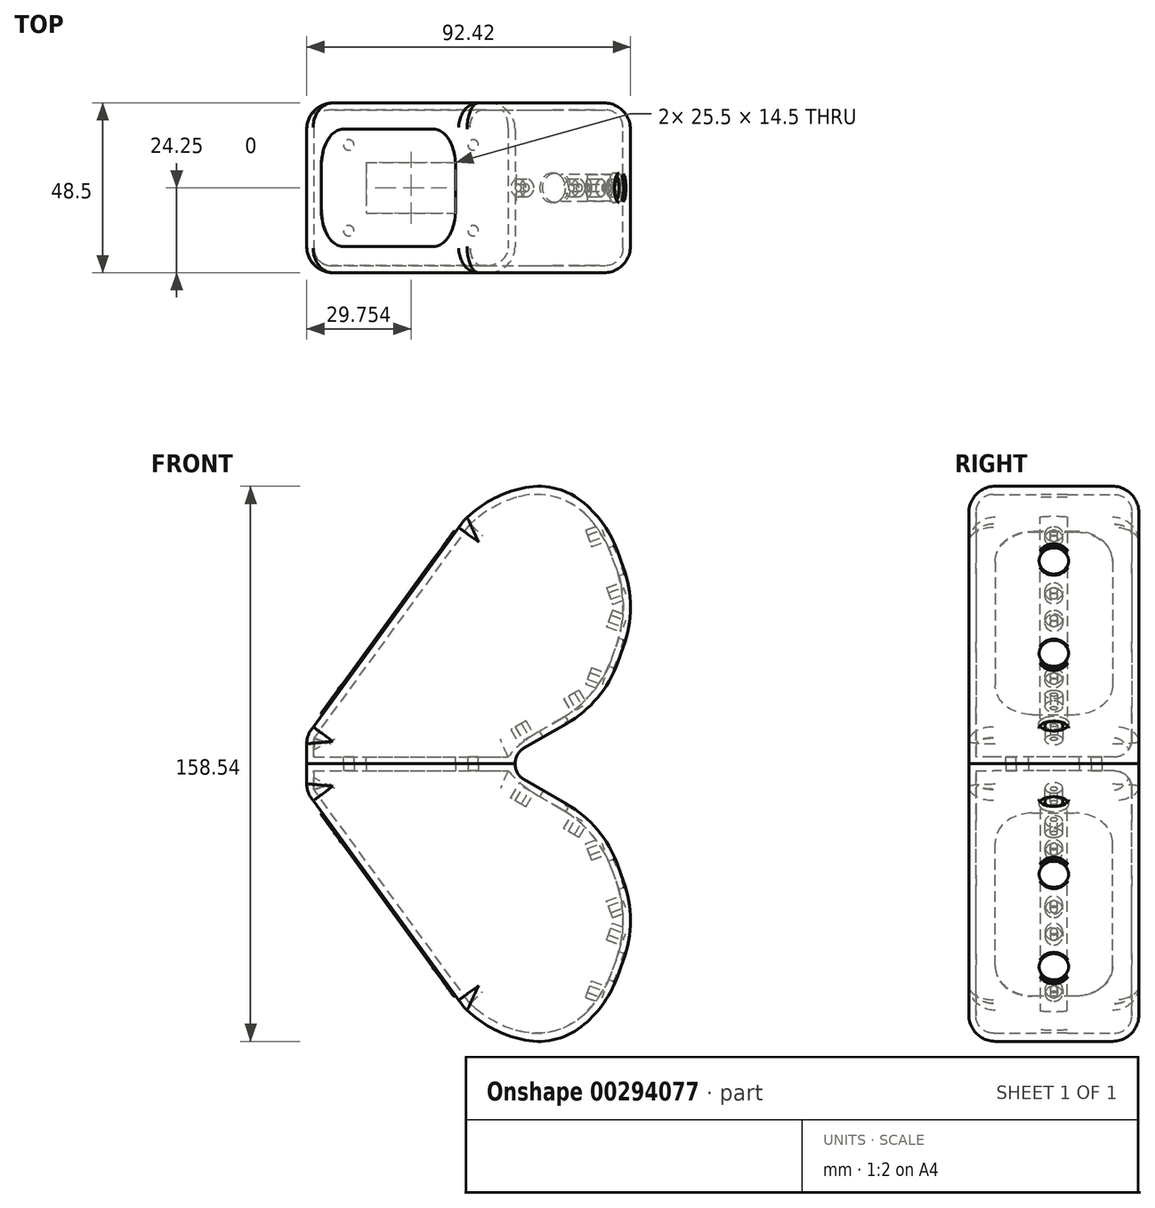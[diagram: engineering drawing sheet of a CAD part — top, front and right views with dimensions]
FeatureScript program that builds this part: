
annotation { "Feature Type Name" : "Feature", "Feature Type Description" : "" }
export const myFeature = defineFeature(function(context is Context, id is Id, definition is map)
    precondition{}
    {
        {
            var Q0;
            Q0=qCreatedBy(makeId("Top.planeOp"),FACE);
            var sketch = newSketch(context, id + "F0", { "sketchPlane" : qUnion([Q0])});
            skLineSegment(sketch, "E0.bottom", {"start": v(-27.46, 14.83) * mm, "end": v(32.04, 14.83) * mm});
            skLineSegment(sketch, "E0.top", {"start": v(-27.46, -33.67) * mm, "end": v(32.04, -33.67) * mm});
            skLineSegment(sketch, "E0.left", {"start": v(-27.46, 14.83) * mm, "end": v(-27.46, -33.67) * mm});
            skLineSegment(sketch, "E0.right", {"start": v(32.04, 14.83) * mm, "end": v(32.04, -33.67) * mm});
            skSolve(sketch);
        }
        {
            var Q0;
            Q0=makeQuery(id+"F0.imprint","IMPRINT",FACE,{"disambiguationData":[TD([[makeQuery(id+"F0.imprint","IMPRINT",EDGE,{"derivedFrom":sQuery(id+"F0.wireOp",EDGE,"E0.bottom")}),-1.0]])]});
            extrude(context, id + "F1", {"entities" : qUnion([Q0]), "depth" : 3 * mm});
        }
        {
            var Q0;
            Q0=makeQuery(id+"F1.opExtrude","SWEPT_FACE",FACE,{"disambiguationData":[OSD([sQuery(id+"F0.wireOp",EDGE,"E0.top")])]});
            var sketch = newSketch(context, id + "F2", { "sketchPlane" : qUnion([Q0])});
            skLineSegment(sketch, "E1", {"start": v(32.04, 3) * mm, "end": v(57.16, 17.5) * mm});
            skLineSegment(sketch, "E2", {"start": v(57.16, 17.5) * mm, "end": v(67.08, 44.75) * mm});
            skLineSegment(sketch, "E3", {"start": v(67.08, 44.75) * mm, "end": v(57.16, 72) * mm});
            skLineSegment(sketch, "E4", {"start": v(44.6, 10.25) * mm, "end": v(61.97, -88.23) * mm, "construction": true});
            skLineSegment(sketch, "E5", {"start": v(44.6, 10.25) * mm, "end": v(121.2, -54.03) * mm, "construction": true});
            skLineSegment(sketch, "E6", {"start": v(62.12, 31.13) * mm, "end": v(138.72, -33.15) * mm, "construction": true});
            skLineSegment(sketch, "E7", {"start": v(62.12, 31.13) * mm, "end": v(162.12, 31.13) * mm, "construction": true});
            skLineSegment(sketch, "E8", {"start": v(62.12, 58.38) * mm, "end": v(162.12, 58.38) * mm, "construction": true});
            skLineSegment(sketch, "E9", {"start": v(62.12, 58.38) * mm, "end": v(138.72, 122.66) * mm, "construction": true});
            skLineSegment(sketch, "E10", {"start": v(32.04, 3) * mm, "end": v(32.04, 5) * mm});
            skLineSegment(sketch, "E11", {"start": v(62.12, 58.38) * mm, "end": v(79.93, 64.86) * mm, "construction": true});
            skLineSegment(sketch, "E12", {"start": v(62.12, 31.13) * mm, "end": v(79.43, 24.82) * mm, "construction": true});
            skLineSegment(sketch, "E13", {"start": v(29.2, 36.93) * mm, "end": v(44.6, 10.25) * mm, "construction": true});
            skLineSegment(sketch, "E14", {"start": v(32.04, 3) * mm, "end": v(32.04, -40.7) * mm, "construction": true});
            skLineSegment(sketch, "E15", {"start": v(32.04, 5) * mm, "end": v(32.04, 48.67) * mm, "construction": true});
            skLineSegment(sketch, "E16", {"start": v(57.16, 72) * mm, "end": v(44.17, 79.5) * mm});
            skLineSegment(sketch, "E17", {"start": v(44.17, 79.5) * mm, "end": v(29.17, 79.5) * mm});
            skLineSegment(sketch, "E18", {"start": v(-27.46, 3) * mm, "end": v(-27.46, 8) * mm});
            skLineSegment(sketch, "E19", {"start": v(29.17, 79.5) * mm, "end": v(17.68, 69.86) * mm});
            skLineSegment(sketch, "E20", {"start": v(17.68, 69.86) * mm, "end": v(-27.46, 8) * mm});
            skSolve(sketch);
        }
        {
            var Q0;
            Q0=makeQuery(id+"F2.imprint","IMPRINT",FACE,{"disambiguationData":[TD([[makeQuery(id+"F2.imprint","IMPRINT",EDGE,{"derivedFrom":sQuery(id+"F2.wireOp",EDGE,"E1")}),1.0]])]});
            var Q1;
            Q1=makeQuery(id+"F1.opExtrude","SWEPT_FACE",FACE,{"disambiguationData":[OSD([sQuery(id+"F0.wireOp",EDGE,"E0.bottom")])]});
            extrude(context, id + "F3", {"entities" : qUnion([Q0]), "operationType" : NewBodyOperationType.ADD, "endBound" : BoundingType.UP_TO_SURFACE, "oppositeDirection" : true, "endBoundEntityFace" : qUnion([Q1]), "depth" : 25 * mm});
        }
        {
            var Q0;
            Q0=makeQuery(id+"F3.opExtrude","SWEPT_FACE",FACE,{"disambiguationData":[OSD([sQuery(id+"F2.wireOp",EDGE,"E20")])]});
            var sketch = newSketch(context, id + "F4", { "sketchPlane" : qUnion([Q0])});
            skLineSegment(sketch, "E21.bottom", {"start": v(25.67, 61.86) * mm, "end": v(-6.83, 61.86) * mm});
            skLineSegment(sketch, "E21.top", {"start": v(25.67, -1.72) * mm, "end": v(-6.83, -1.72) * mm});
            skLineSegment(sketch, "E21.left", {"start": v(25.67, 61.86) * mm, "end": v(25.67, -1.72) * mm});
            skLineSegment(sketch, "E21.right", {"start": v(-6.83, 61.86) * mm, "end": v(-6.83, -1.72) * mm});
            skSolve(sketch);
        }
        {
            var Q0;
            Q0=makeQuery(id+"F4.imprint","IMPRINT",FACE,{"disambiguationData":[TD([[makeQuery(id+"F4.imprint","IMPRINT",EDGE,{"derivedFrom":sQuery(id+"F4.wireOp",EDGE,"E21.bottom")}),1.0]])]});
            extrude(context, id + "F5", {"entities" : qUnion([Q0]), "operationType" : NewBodyOperationType.REMOVE, "oppositeDirection" : true, "depth" : 2 * mm});
        }
        {
            var Q0;
            Q0=makeQuery(id+"F5.boolean.opBoolean","COPY",FACE,{"derivedFrom":makeQuery(id+"F5.opExtrude","CAP_FACE",FACE,{"disambiguationData":[OSD([sQuery(id+"F4.wireOp",EDGE,"E21.bottom"),sQuery(id+"F4.wireOp",EDGE,"E21.top"),sQuery(id+"F4.wireOp",EDGE,"E21.left"),sQuery(id+"F4.wireOp",EDGE,"E21.right")])],"isStart":false})});
            shell(context, id + "F6", {"entities" : qUnion([Q0]), "thickness" : 2 * mm});
        }
        {
            var Q0;
            Q0=makeQuery(id+"F6.opShell","OFFSET_FACE",FACE,{"disambiguationData":[OSD([sQuery(id+"F2.wireOp",EDGE,"E1")])]});
            var sketch = newSketch(context, id + "F7", { "sketchPlane" : qUnion([Q0])});
            skLineSegment(sketch, "E22.0", {"start": v(28.1, 12.83) * mm, "end": v(28.1, -31.67) * mm});
            skLineSegment(sketch, "E23.0", {"start": v(57.52, 12.83) * mm, "end": v(57.52, -31.67) * mm});
            skLineSegment(sketch, "E24", {"start": v(28.1, -9.42) * mm, "end": v(57.52, -9.42) * mm, "construction": true});
            skCircle(sketch, "E25", {"center": v(42.8, -9.42) * mm, "radius": 4.25 * mm});
            skCircle(sketch, "E26", {"center": v(34.06, -9.42) * mm, "radius": 1 * mm});
            skCircle(sketch, "E27", {"center": v(34.06, -9.42) * mm, "radius": 2.5 * mm});
            skCircle(sketch, "E28", {"center": v(51.56, -9.42) * mm, "radius": 1 * mm});
            skCircle(sketch, "E29", {"center": v(51.56, -9.42) * mm, "radius": 2.5 * mm});
            skSolve(sketch);
        }
        {
            var Q0;
            Q0=makeQuery(id+"F6.opShell","OFFSET_FACE",FACE,{"disambiguationData":[OSD([sQuery(id+"F2.wireOp",EDGE,"E2")])]});
            var sketch = newSketch(context, id + "F8", { "sketchPlane" : qUnion([Q0])});
            skLineSegment(sketch, "E30.0", {"start": v(-12.83, 36.72) * mm, "end": v(31.67, 36.72) * mm});
            skLineSegment(sketch, "E31.0", {"start": v(-12.83, 64.27) * mm, "end": v(31.67, 64.27) * mm});
            skLineSegment(sketch, "E32", {"start": v(9.42, 36.72) * mm, "end": v(9.42, 64.27) * mm, "construction": true});
            skCircle(sketch, "E33", {"center": v(9.42, 50.5) * mm, "radius": 4.25 * mm});
            skCircle(sketch, "E34", {"center": v(9.42, 41.74) * mm, "radius": 1 * mm});
            skCircle(sketch, "E35", {"center": v(9.42, 41.74) * mm, "radius": 2.5 * mm});
            skCircle(sketch, "E36", {"center": v(9.42, 59.24) * mm, "radius": 1 * mm});
            skCircle(sketch, "E37", {"center": v(9.42, 59.24) * mm, "radius": 2.5 * mm});
            skSolve(sketch);
        }
        {
            var Q0;
            Q0=makeQuery(id+"F6.opShell","OFFSET_FACE",FACE,{"disambiguationData":[OSD([sQuery(id+"F2.wireOp",EDGE,"E3")])]});
            var sketch = newSketch(context, id + "F9", { "sketchPlane" : qUnion([Q0])});
            skLineSegment(sketch, "E38", {"start": v(9.42, 19.84) * mm, "end": v(9.42, 47.38) * mm, "construction": true});
            skCircle(sketch, "E39", {"center": v(9.42, 33.61) * mm, "radius": 4.25 * mm});
            skCircle(sketch, "E40", {"center": v(9.42, 42.36) * mm, "radius": 1 * mm});
            skCircle(sketch, "E41", {"center": v(9.42, 42.36) * mm, "radius": 2.5 * mm});
            skCircle(sketch, "E42", {"center": v(9.42, 24.86) * mm, "radius": 1 * mm});
            skCircle(sketch, "E43", {"center": v(9.42, 24.86) * mm, "radius": 2.5 * mm});
            skSolve(sketch);
        }
        {
            var Q0;
            Q0=makeQuery(id+"F7.imprint","IMPRINT",FACE,{"disambiguationData":[TD([[makeQuery(id+"F7.imprint","IMPRINT",EDGE,{"derivedFrom":sQuery(id+"F7.wireOp",EDGE,"E25")}),1.0]])]});
            extrude(context, id + "F10", {"entities" : qUnion([Q0]), "operationType" : NewBodyOperationType.REMOVE, "oppositeDirection" : true, "depth" : 25 * mm});
        }
        {
            var Q0;
            Q0=makeQuery(id+"F8.imprint","IMPRINT",FACE,{"disambiguationData":[TD([[makeQuery(id+"F8.imprint","IMPRINT",EDGE,{"derivedFrom":sQuery(id+"F8.wireOp",EDGE,"E33")}),1.0]])]});
            extrude(context, id + "F11", {"entities" : qUnion([Q0]), "operationType" : NewBodyOperationType.REMOVE, "oppositeDirection" : true, "depth" : 25 * mm});
        }
        {
            var Q0;
            Q0=makeQuery(id+"F9.imprint","IMPRINT",FACE,{"disambiguationData":[TD([[makeQuery(id+"F9.imprint","IMPRINT",EDGE,{"derivedFrom":sQuery(id+"F9.wireOp",EDGE,"E39")}),1.0]])]});
            extrude(context, id + "F12", {"entities" : qUnion([Q0]), "operationType" : NewBodyOperationType.REMOVE, "oppositeDirection" : true, "depth" : 25 * mm});
        }
        {
            var Q0;
            Q0=makeQuery(id+"F7.imprint","IMPRINT",FACE,{"disambiguationData":[TD([[makeQuery(id+"F7.imprint","IMPRINT",EDGE,{"derivedFrom":sQuery(id+"F7.wireOp",EDGE,"E26")}),-1.0]])]});
            var Q1;
            Q1=makeQuery(id+"F7.imprint","IMPRINT",FACE,{"disambiguationData":[TD([[makeQuery(id+"F7.imprint","IMPRINT",EDGE,{"derivedFrom":sQuery(id+"F7.wireOp",EDGE,"E28")}),-1.0]])]});
            extrude(context, id + "F13", {"entities" : qUnion([Q0, Q1]), "operationType" : NewBodyOperationType.ADD, "depth" : 4.5 * mm});
        }
        {
            var Q0;
            Q0=makeQuery(id+"F8.imprint","IMPRINT",FACE,{"disambiguationData":[TD([[makeQuery(id+"F8.imprint","IMPRINT",EDGE,{"derivedFrom":sQuery(id+"F8.wireOp",EDGE,"E34")}),-1.0]])]});
            var Q1;
            Q1=makeQuery(id+"F8.imprint","IMPRINT",FACE,{"disambiguationData":[TD([[makeQuery(id+"F8.imprint","IMPRINT",EDGE,{"derivedFrom":sQuery(id+"F8.wireOp",EDGE,"E36")}),-1.0]])]});
            extrude(context, id + "F14", {"entities" : qUnion([Q0, Q1]), "operationType" : NewBodyOperationType.ADD, "depth" : 4.5 * mm});
        }
        {
            var Q0;
            Q0=makeQuery(id+"F9.imprint","IMPRINT",FACE,{"disambiguationData":[TD([[makeQuery(id+"F9.imprint","IMPRINT",EDGE,{"derivedFrom":sQuery(id+"F9.wireOp",EDGE,"E42")}),-1.0]])]});
            var Q1;
            Q1=makeQuery(id+"F9.imprint","IMPRINT",FACE,{"disambiguationData":[TD([[makeQuery(id+"F9.imprint","IMPRINT",EDGE,{"derivedFrom":sQuery(id+"F9.wireOp",EDGE,"E40")}),-1.0]])]});
            extrude(context, id + "F15", {"entities" : qUnion([Q0, Q1]), "operationType" : NewBodyOperationType.ADD, "depth" : 4.5 * mm});
        }
        {
            var Q0;
            Q0=makeQuery(id+"F6.opShell","OFFSET_FACE",FACE,{"disambiguationData":[OSD([sQuery(id+"F0.wireOp",EDGE,"E0.bottom"),sQuery(id+"F0.wireOp",EDGE,"E0.top"),sQuery(id+"F0.wireOp",EDGE,"E0.left"),sQuery(id+"F0.wireOp",EDGE,"E0.right")])]});
            var sketch = newSketch(context, id + "F16", { "sketchPlane" : qUnion([Q0])});
            skLineSegment(sketch, "E44.bottom", {"start": v(-10.46, -2.17) * mm, "end": v(15.04, -2.17) * mm});
            skLineSegment(sketch, "E44.top", {"start": v(-10.46, -16.67) * mm, "end": v(15.04, -16.67) * mm});
            skLineSegment(sketch, "E44.left", {"start": v(-10.46, -2.17) * mm, "end": v(-10.46, -16.67) * mm});
            skLineSegment(sketch, "E44.right", {"start": v(15.04, -2.17) * mm, "end": v(15.04, -16.67) * mm});
            skSolve(sketch);
        }
        {
            var Q0;
            Q0=makeQuery(id+"F16.imprint","IMPRINT",FACE,{"disambiguationData":[TD([[makeQuery(id+"F16.imprint","IMPRINT",EDGE,{"derivedFrom":sQuery(id+"F16.wireOp",EDGE,"E44.bottom")}),-1.0]])]});
            extrude(context, id + "F17", {"entities" : qUnion([Q0]), "operationType" : NewBodyOperationType.REMOVE, "oppositeDirection" : true, "depth" : 25 * mm});
        }
        {
            var Q0;
            Q0=makeQuery(id+"F6.opShell","OFFSET_EDGE",EDGE,{"disambiguationData":[OSD([sQuery(id+"F2.wireOp",EDGE,"E1"),sQuery(id+"F2.wireOp",EDGE,"E2")])]});
            var Q1;
            Q1=makeQuery(id+"F6.opShell","OFFSET_EDGE",EDGE,{"disambiguationData":[OSD([sQuery(id+"F2.wireOp",EDGE,"E2"),sQuery(id+"F2.wireOp",EDGE,"E3")])]});
            var Q2;
            Q2=makeQuery(id+"F6.opShell","OFFSET_EDGE",EDGE,{"disambiguationData":[OSD([sQuery(id+"F2.wireOp",EDGE,"E3"),sQuery(id+"F2.wireOp",EDGE,"E16")])]});
            var Q3;
            Q3=makeQuery(id+"F3.opExtrude","SWEPT_EDGE",EDGE,{"disambiguationData":[OSD([sQuery(id+"F2.wireOp",EDGE,"E1"),sQuery(id+"F2.wireOp",EDGE,"E2")])]});
            var Q4;
            Q4=makeQuery(id+"F3.opExtrude","SWEPT_EDGE",EDGE,{"disambiguationData":[OSD([sQuery(id+"F2.wireOp",EDGE,"E2"),sQuery(id+"F2.wireOp",EDGE,"E3")])]});
            var Q5;
            Q5=makeQuery(id+"F3.opExtrude","SWEPT_EDGE",EDGE,{"disambiguationData":[OSD([sQuery(id+"F2.wireOp",EDGE,"E3"),sQuery(id+"F2.wireOp",EDGE,"E16")])]});
            var Q6;
            Q6=makeQuery(id+"F6.opShell","OFFSET_EDGE",EDGE,{"disambiguationData":[OSD([sQuery(id+"F0.wireOp",EDGE,"E0.top"),sQuery(id+"F0.wireOp",EDGE,"E0.right"),sQuery(id+"F2.wireOp",EDGE,"E1")])]});
            var Q7;
            {var subQ0=sQuery(id+"F2.wireOp",EDGE,"E1");var subQ1=sQuery(id+"F0.wireOp",EDGE,"E0.right");Q7=makeQuery(id+"F20.opFillet","BLEND_EDGE",EDGE,{"blendedFrom":[makeQuery(id+"F3.boolean.opBoolean","MERGE",EDGE,{"derivedFrom":[makeQuery(id+"F1.opExtrude","CAP_EDGE",EDGE,{"disambiguationData":[OSD([subQ1])],"isStart":false}),makeQuery(id+"F3.opExtrude","SWEPT_EDGE",EDGE,{"disambiguationData":[OSD([sQuery(id+"F0.wireOp",EDGE,"E0.top"),subQ1,subQ0])]})]}),makeQuery(id+"F3.opExtrude","SWEPT_FACE",FACE,{"disambiguationData":[OSD([subQ0])]})],"blendedInto":[makeQuery(id+"F3.opExtrude","SWEPT_FACE",FACE,{"disambiguationData":[OSD([subQ0])]})]});}
            var Q8;
            Q8=makeQuery(id+"F3.opExtrude","SWEPT_EDGE",EDGE,{"disambiguationData":[OSD([sQuery(id+"F2.wireOp",EDGE,"E17"),sQuery(id+"F2.wireOp",EDGE,"E19")])]});
            var Q9;
            Q9=makeQuery(id+"F6.opShell","OFFSET_EDGE",EDGE,{"disambiguationData":[OSD([sQuery(id+"F2.wireOp",EDGE,"E17"),sQuery(id+"F2.wireOp",EDGE,"E19")])]});
            fillet(context, id + "F18", {"entities" : qUnion([Q0, Q1, Q2, Q3, Q4, Q5, Q6, Q7, Q8, Q9]), "radius" : 33 * mm, "tangentPropagation" : true, "allowEdgeOverflow" : false});
        }
        {
            var Q0;
            Q0=makeQuery(id+"F6.opShell","OFFSET_EDGE",EDGE,{"disambiguationData":[OSD([sQuery(id+"F2.wireOp",EDGE,"E16"),sQuery(id+"F2.wireOp",EDGE,"E17")])]});
            var Q1;
            Q1=makeQuery(id+"F3.opExtrude","SWEPT_EDGE",EDGE,{"disambiguationData":[OSD([sQuery(id+"F2.wireOp",EDGE,"E16"),sQuery(id+"F2.wireOp",EDGE,"E17")])]});
            fillet(context, id + "F19", {"entities" : qUnion([Q0, Q1]), "radius" : 20 * mm, "tangentPropagation" : true, "allowEdgeOverflow" : false});
        }
        {
            var Q0;
            {var subQ0=sQuery(id+"F0.wireOp",EDGE,"E0.right");Q0=makeQuery(id+"F3.boolean.opBoolean","MERGE",EDGE,{"derivedFrom":[makeQuery(id+"F1.opExtrude","CAP_EDGE",EDGE,{"disambiguationData":[OSD([subQ0])],"isStart":false}),makeQuery(id+"F3.opExtrude","SWEPT_EDGE",EDGE,{"disambiguationData":[OSD([sQuery(id+"F0.wireOp",EDGE,"E0.top"),subQ0,sQuery(id+"F2.wireOp",EDGE,"E1")])]})]});}
            var Q1;
            Q1=makeQuery(id+"F6.opShell","OFFSET_EDGE",EDGE,{"disambiguationData":[OSD([sQuery(id+"F2.wireOp",EDGE,"E1")])]});
            var Q2;
            Q2=makeQuery(id+"F6.opShell","OFFSET_EDGE",EDGE,{"disambiguationData":[OSD([sQuery(id+"F0.wireOp",EDGE,"E0.bottom"),sQuery(id+"F2.wireOp",EDGE,"E1")])]});
            var Q3;
            Q3=makeQuery(id+"F6.opShell","OFFSET_EDGE",EDGE,{"disambiguationData":[OSD([sQuery(id+"F0.wireOp",EDGE,"E0.bottom"),sQuery(id+"F0.wireOp",EDGE,"E0.right")])]});
            var Q4;
            Q4=makeQuery(id+"F6.opShell","OFFSET_EDGE",EDGE,{"disambiguationData":[OSD([sQuery(id+"F0.wireOp",EDGE,"E0.top"),sQuery(id+"F0.wireOp",EDGE,"E0.right")])]});
            var Q5;
            Q5=makeQuery(id+"F6.opShell","OFFSET_EDGE",EDGE,{"disambiguationData":[OSD([sQuery(id+"F0.wireOp",EDGE,"E0.bottom"),sQuery(id+"F2.wireOp",EDGE,"E2")])]});
            var Q6;
            Q6=makeQuery(id+"F6.opShell","OFFSET_EDGE",EDGE,{"disambiguationData":[OSD([sQuery(id+"F0.wireOp",EDGE,"E0.bottom"),sQuery(id+"F2.wireOp",EDGE,"E3")])]});
            var Q7;
            Q7=makeQuery(id+"F6.opShell","OFFSET_EDGE",EDGE,{"disambiguationData":[OSD([sQuery(id+"F0.wireOp",EDGE,"E0.bottom"),sQuery(id+"F2.wireOp",EDGE,"E16")])]});
            var Q8;
            Q8=makeQuery(id+"F6.opShell","OFFSET_EDGE",EDGE,{"disambiguationData":[OSD([sQuery(id+"F0.wireOp",EDGE,"E0.bottom"),sQuery(id+"F2.wireOp",EDGE,"E17")])]});
            var Q9;
            Q9=makeQuery(id+"F6.opShell","OFFSET_EDGE",EDGE,{"disambiguationData":[OSD([sQuery(id+"F0.wireOp",EDGE,"E0.bottom"),sQuery(id+"F0.wireOp",EDGE,"E0.left"),sQuery(id+"F2.wireOp",EDGE,"E18")])]});
            var Q10;
            Q10=makeQuery(id+"F6.opShell","OFFSET_EDGE",EDGE,{"disambiguationData":[OSD([sQuery(id+"F0.wireOp",EDGE,"E0.top"),sQuery(id+"F0.wireOp",EDGE,"E0.left"),sQuery(id+"F2.wireOp",EDGE,"E18")])]});
            var Q11;
            Q11=makeQuery(id+"F6.opShell","OFFSET_EDGE",EDGE,{"disambiguationData":[OSD([sQuery(id+"F2.wireOp",EDGE,"E2")])]});
            var Q12;
            Q12=makeQuery(id+"F6.opShell","OFFSET_EDGE",EDGE,{"disambiguationData":[OSD([sQuery(id+"F2.wireOp",EDGE,"E3")])]});
            var Q13;
            Q13=makeQuery(id+"F6.opShell","OFFSET_EDGE",EDGE,{"disambiguationData":[OSD([sQuery(id+"F2.wireOp",EDGE,"E16")])]});
            var Q14;
            Q14=makeQuery(id+"F6.opShell","OFFSET_EDGE",EDGE,{"disambiguationData":[OSD([sQuery(id+"F2.wireOp",EDGE,"E17")])]});
            var Q15;
            {var subQ0=sQuery(id+"F2.wireOp",EDGE,"E16");Q15=makeQuery(id+"F18.opFillet","BLEND_EDGE",EDGE,{"disambiguationData":[OD(0.0)],"blendedFrom":[makeQuery(id+"F6.opShell","OFFSET_EDGE",EDGE,{"disambiguationData":[OSD([sQuery(id+"F2.wireOp",EDGE,"E3"),subQ0])]}),makeQuery(id+"F6.opShell","OFFSET_EDGE",EDGE,{"disambiguationData":[OSD([subQ0,sQuery(id+"F2.wireOp",EDGE,"E17")])]})],"blendedInto":[]});}
            var Q16;
            Q16=makeQuery(id+"F6.opShell","OFFSET_EDGE",EDGE,{"disambiguationData":[OSD([sQuery(id+"F2.wireOp",EDGE,"E20")])]});
            var Q17;
            {var subQ0=sQuery(id+"F2.wireOp",EDGE,"E19");var subQ1=sQuery(id+"F2.wireOp",EDGE,"E17");Q17=makeQuery(id+"F18.opFillet","BLEND_EDGE",EDGE,{"blendedFrom":[makeQuery(id+"F6.opShell","OFFSET_EDGE",EDGE,{"disambiguationData":[OSD([subQ1,subQ0])]}),makeQuery(id+"F6.opShell","OFFSET_FACE",FACE,{"disambiguationData":[OSD([sQuery(id+"F0.wireOp",EDGE,"E0.top"),sQuery(id+"F2.wireOp",EDGE,"E1"),sQuery(id+"F2.wireOp",EDGE,"E2"),sQuery(id+"F2.wireOp",EDGE,"E3"),sQuery(id+"F2.wireOp",EDGE,"E16"),subQ1,sQuery(id+"F2.wireOp",EDGE,"E18"),subQ0,sQuery(id+"F2.wireOp",EDGE,"E20")])]})],"blendedInto":[makeQuery(id+"F6.opShell","OFFSET_FACE",FACE,{"disambiguationData":[OSD([sQuery(id+"F0.wireOp",EDGE,"E0.top"),sQuery(id+"F2.wireOp",EDGE,"E1"),sQuery(id+"F2.wireOp",EDGE,"E2"),sQuery(id+"F2.wireOp",EDGE,"E3"),sQuery(id+"F2.wireOp",EDGE,"E16"),subQ1,sQuery(id+"F2.wireOp",EDGE,"E18"),subQ0,sQuery(id+"F2.wireOp",EDGE,"E20")])]})]});}
            var Q18;
            Q18=makeQuery(id+"F6.opShell","OFFSET_EDGE",EDGE,{"disambiguationData":[OSD([sQuery(id+"F0.wireOp",EDGE,"E0.bottom"),sQuery(id+"F2.wireOp",EDGE,"E20")])]});
            var Q19;
            Q19=makeQuery(id+"F18.opFillet","BLEND_EDGE",EDGE,{"blendedFrom":[makeQuery(id+"F6.opShell","OFFSET_EDGE",EDGE,{"disambiguationData":[OSD([sQuery(id+"F2.wireOp",EDGE,"E17"),sQuery(id+"F2.wireOp",EDGE,"E19")])]}),makeQuery(id+"F6.opShell","OFFSET_FACE",FACE,{"disambiguationData":[OSD([sQuery(id+"F0.wireOp",EDGE,"E0.bottom")])]})],"blendedInto":[makeQuery(id+"F6.opShell","OFFSET_FACE",FACE,{"disambiguationData":[OSD([sQuery(id+"F0.wireOp",EDGE,"E0.bottom")])]})]});
            var Q20;
            Q20=makeQuery(id+"F18.opFillet","BLEND_EDGE",EDGE,{"blendedFrom":[makeQuery(id+"F6.opShell","OFFSET_EDGE",EDGE,{"disambiguationData":[OSD([sQuery(id+"F2.wireOp",EDGE,"E16"),sQuery(id+"F2.wireOp",EDGE,"E17")])]}),makeQuery(id+"F6.opShell","OFFSET_FACE",FACE,{"disambiguationData":[OSD([sQuery(id+"F0.wireOp",EDGE,"E0.bottom")])]})],"blendedInto":[makeQuery(id+"F6.opShell","OFFSET_FACE",FACE,{"disambiguationData":[OSD([sQuery(id+"F0.wireOp",EDGE,"E0.bottom")])]})]});
            var Q21;
            {var subQ0=sQuery(id+"F2.wireOp",EDGE,"E17");var subQ1=sQuery(id+"F2.wireOp",EDGE,"E16");Q21=makeQuery(id+"F18.opFillet","BLEND_EDGE",EDGE,{"blendedFrom":[makeQuery(id+"F6.opShell","OFFSET_EDGE",EDGE,{"disambiguationData":[OSD([subQ1,subQ0])]}),makeQuery(id+"F6.opShell","OFFSET_FACE",FACE,{"disambiguationData":[OSD([sQuery(id+"F0.wireOp",EDGE,"E0.top"),sQuery(id+"F2.wireOp",EDGE,"E1"),sQuery(id+"F2.wireOp",EDGE,"E2"),sQuery(id+"F2.wireOp",EDGE,"E3"),subQ1,subQ0,sQuery(id+"F2.wireOp",EDGE,"E18"),sQuery(id+"F2.wireOp",EDGE,"E19"),sQuery(id+"F2.wireOp",EDGE,"E20")])]})],"blendedInto":[makeQuery(id+"F6.opShell","OFFSET_FACE",FACE,{"disambiguationData":[OSD([sQuery(id+"F0.wireOp",EDGE,"E0.top"),sQuery(id+"F2.wireOp",EDGE,"E1"),sQuery(id+"F2.wireOp",EDGE,"E2"),sQuery(id+"F2.wireOp",EDGE,"E3"),subQ1,subQ0,sQuery(id+"F2.wireOp",EDGE,"E18"),sQuery(id+"F2.wireOp",EDGE,"E19"),sQuery(id+"F2.wireOp",EDGE,"E20")])]})]});}
            fillet(context, id + "F20", {"entities" : qUnion([Q0, Q1, Q2, Q3, Q4, Q5, Q6, Q7, Q8, Q9, Q10, Q11, Q12, Q13, Q14, Q15, Q16, Q17, Q18, Q19, Q20, Q21]), "radius" : 5 * mm, "tangentPropagation" : true, "allowEdgeOverflow" : false});
        }
        {
            var Q0;
            {var subQ0=sQuery(id+"F0.wireOp",EDGE,"E0.bottom");var subQ1=sQuery(id+"F0.wireOp",EDGE,"E0.right");Q0=makeQuery(id+"F20.opFillet","BLEND_EDGE",EDGE,{"blendedFrom":[makeQuery(id+"F3.boolean.opBoolean","MERGE",EDGE,{"derivedFrom":[makeQuery(id+"F1.opExtrude","CAP_EDGE",EDGE,{"disambiguationData":[OSD([subQ1])],"isStart":false}),makeQuery(id+"F3.opExtrude","SWEPT_EDGE",EDGE,{"disambiguationData":[OSD([sQuery(id+"F0.wireOp",EDGE,"E0.top"),subQ1,sQuery(id+"F2.wireOp",EDGE,"E1")])]})]}),makeQuery(id+"F3.boolean.opBoolean","MERGE",FACE,{"derivedFrom":[makeQuery(id+"F1.opExtrude","SWEPT_FACE",FACE,{"disambiguationData":[OSD([subQ0])]}),makeQuery(id+"F3.opExtrude","CAP_FACE",FACE,{"disambiguationData":[OSD([subQ0])],"isStart":false})]})],"blendedInto":[makeQuery(id+"F3.boolean.opBoolean","MERGE",FACE,{"derivedFrom":[makeQuery(id+"F1.opExtrude","SWEPT_FACE",FACE,{"disambiguationData":[OSD([subQ0])]}),makeQuery(id+"F3.opExtrude","CAP_FACE",FACE,{"disambiguationData":[OSD([subQ0])],"isStart":false})]})]});}
            var Q1;
            {var subQ0=sQuery(id+"F2.wireOp",EDGE,"E1");var subQ1=sQuery(id+"F0.wireOp",EDGE,"E0.top");var subQ2=sQuery(id+"F0.wireOp",EDGE,"E0.right");Q1=makeQuery(id+"F20.opFillet","BLEND_EDGE",EDGE,{"blendedFrom":[makeQuery(id+"F3.boolean.opBoolean","MERGE",EDGE,{"derivedFrom":[makeQuery(id+"F1.opExtrude","CAP_EDGE",EDGE,{"disambiguationData":[OSD([subQ2])],"isStart":false}),makeQuery(id+"F3.opExtrude","SWEPT_EDGE",EDGE,{"disambiguationData":[OSD([subQ1,subQ2,subQ0])]})]}),makeQuery(id+"F3.boolean.opBoolean","MERGE",FACE,{"derivedFrom":[makeQuery(id+"F1.opExtrude","SWEPT_FACE",FACE,{"disambiguationData":[OSD([subQ1])]}),makeQuery(id+"F3.opExtrude","CAP_FACE",FACE,{"disambiguationData":[OSD([subQ1,subQ0,sQuery(id+"F2.wireOp",EDGE,"E2"),sQuery(id+"F2.wireOp",EDGE,"E3"),sQuery(id+"F2.wireOp",EDGE,"E16"),sQuery(id+"F2.wireOp",EDGE,"E17"),sQuery(id+"F2.wireOp",EDGE,"E18"),sQuery(id+"F2.wireOp",EDGE,"AT5yo8GT-OiPT-c7XB-dJuP-BCaW8Njyvu8z")])],"isStart":true})]})],"blendedInto":[makeQuery(id+"F3.boolean.opBoolean","MERGE",FACE,{"derivedFrom":[makeQuery(id+"F1.opExtrude","SWEPT_FACE",FACE,{"disambiguationData":[OSD([subQ1])]}),makeQuery(id+"F3.opExtrude","CAP_FACE",FACE,{"disambiguationData":[OSD([subQ1,subQ0,sQuery(id+"F2.wireOp",EDGE,"E2"),sQuery(id+"F2.wireOp",EDGE,"E3"),sQuery(id+"F2.wireOp",EDGE,"E16"),sQuery(id+"F2.wireOp",EDGE,"E17"),sQuery(id+"F2.wireOp",EDGE,"E18"),sQuery(id+"F2.wireOp",EDGE,"AT5yo8GT-OiPT-c7XB-dJuP-BCaW8Njyvu8z")])],"isStart":true})]})]});}
            var Q2;
            Q2=makeQuery(id+"F3.opExtrude","TWEAK_EDGE",EDGE,{"derivedFrom":[makeQuery(id+"F1.opExtrude","SWEPT_FACE",FACE,{"disambiguationData":[OSD([sQuery(id+"F0.wireOp",EDGE,"E0.bottom")])]}),makeQuery(id+"F2.imprint","IMPRINT",EDGE,{"derivedFrom":sQuery(id+"F2.wireOp",EDGE,"E2")})]});
            var Q3;
            Q3=makeQuery(id+"F3.opExtrude","CAP_EDGE",EDGE,{"disambiguationData":[OSD([sQuery(id+"F2.wireOp",EDGE,"E2")])],"isStart":true});
            var Q4;
            Q4=makeQuery(id+"F3.opExtrude","CAP_EDGE",EDGE,{"disambiguationData":[OSD([sQuery(id+"F2.wireOp",EDGE,"E3")])],"isStart":true});
            var Q5;
            Q5=makeQuery(id+"F3.opExtrude","TWEAK_EDGE",EDGE,{"derivedFrom":[makeQuery(id+"F1.opExtrude","SWEPT_FACE",FACE,{"disambiguationData":[OSD([sQuery(id+"F0.wireOp",EDGE,"E0.bottom")])]}),makeQuery(id+"F2.imprint","IMPRINT",EDGE,{"derivedFrom":sQuery(id+"F2.wireOp",EDGE,"E3")})]});
            var Q6;
            Q6=makeQuery(id+"F3.opExtrude","TWEAK_EDGE",EDGE,{"derivedFrom":[makeQuery(id+"F1.opExtrude","SWEPT_FACE",FACE,{"disambiguationData":[OSD([sQuery(id+"F0.wireOp",EDGE,"E0.bottom")])]}),makeQuery(id+"F2.imprint","IMPRINT",EDGE,{"derivedFrom":sQuery(id+"F2.wireOp",EDGE,"E16")})]});
            var Q7;
            Q7=makeQuery(id+"F3.opExtrude","TWEAK_EDGE",EDGE,{"derivedFrom":[makeQuery(id+"F1.opExtrude","SWEPT_FACE",FACE,{"disambiguationData":[OSD([sQuery(id+"F0.wireOp",EDGE,"E0.bottom")])]}),makeQuery(id+"F2.imprint","IMPRINT",EDGE,{"derivedFrom":sQuery(id+"F2.wireOp",EDGE,"E17")})]});
            var Q8;
            Q8=makeQuery(id+"F3.opExtrude","CAP_EDGE",EDGE,{"disambiguationData":[OSD([sQuery(id+"F2.wireOp",EDGE,"E16")])],"isStart":true});
            var Q9;
            Q9=makeQuery(id+"F3.opExtrude","CAP_EDGE",EDGE,{"disambiguationData":[OSD([sQuery(id+"F2.wireOp",EDGE,"E17")])],"isStart":true});
            var Q10;
            {var subQ0=sQuery(id+"F0.wireOp",EDGE,"E0.bottom");Q10=makeQuery(id+"F3.boolean.opBoolean","MERGE",EDGE,{"derivedFrom":[makeQuery(id+"F1.opExtrude","SWEPT_EDGE",EDGE,{"disambiguationData":[OSD([subQ0,sQuery(id+"F0.wireOp",EDGE,"E0.left")])]}),makeQuery(id+"F3.opExtrude","TWEAK_EDGE",EDGE,{"derivedFrom":[makeQuery(id+"F1.opExtrude","SWEPT_FACE",FACE,{"disambiguationData":[OSD([subQ0])]}),makeQuery(id+"F2.imprint","IMPRINT",EDGE,{"derivedFrom":sQuery(id+"F2.wireOp",EDGE,"E18")})]})]});}
            var Q11;
            Q11=makeQuery(id+"F3.boolean.opBoolean","MERGE",EDGE,{"derivedFrom":[makeQuery(id+"F1.opExtrude","SWEPT_EDGE",EDGE,{"disambiguationData":[OSD([sQuery(id+"F0.wireOp",EDGE,"E0.top"),sQuery(id+"F0.wireOp",EDGE,"E0.left")])]}),makeQuery(id+"F3.opExtrude","CAP_EDGE",EDGE,{"disambiguationData":[OSD([sQuery(id+"F2.wireOp",EDGE,"E18")])],"isStart":true})]});
            var Q12;
            Q12=makeQuery(id+"F3.opExtrude","CAP_EDGE",EDGE,{"disambiguationData":[OSD([sQuery(id+"F2.wireOp",EDGE,"E19")])],"isStart":true});
            var Q13;
            Q13=makeQuery(id+"F3.opExtrude","TWEAK_EDGE",EDGE,{"derivedFrom":[makeQuery(id+"F1.opExtrude","SWEPT_FACE",FACE,{"disambiguationData":[OSD([sQuery(id+"F0.wireOp",EDGE,"E0.bottom")])]}),makeQuery(id+"F2.imprint","IMPRINT",EDGE,{"derivedFrom":sQuery(id+"F2.wireOp",EDGE,"E19")})]});
            var Q14;
            Q14=makeQuery(id+"F6.opShell","OFFSET_EDGE",EDGE,{"disambiguationData":[OSD([sQuery(id+"F2.wireOp",EDGE,"E19")])]});
            fillet(context, id + "F21", {"entities" : qUnion([Q0, Q1, Q2, Q3, Q4, Q5, Q6, Q7, Q8, Q9, Q10, Q11, Q12, Q13, Q14]), "radius" : 7.5 * mm, "tangentPropagation" : true, "allowEdgeOverflow" : false});
        }
        {
            var Q0;
            Q0=makeQuery(id+"F6.opShell","OFFSET_FACE",FACE,{"disambiguationData":[OSD([sQuery(id+"F0.wireOp",EDGE,"E0.bottom"),sQuery(id+"F0.wireOp",EDGE,"E0.top"),sQuery(id+"F0.wireOp",EDGE,"E0.left"),sQuery(id+"F0.wireOp",EDGE,"E0.right")])]});
            var sketch = newSketch(context, id + "F22", { "sketchPlane" : qUnion([Q0])});
            skCircle(sketch, "E45", {"center": v(-15.46, 2.83) * mm, "radius": 1.5 * mm});
            skCircle(sketch, "E46", {"center": v(20.04, 2.83) * mm, "radius": 1.5 * mm});
            skCircle(sketch, "E47", {"center": v(20.04, -21.67) * mm, "radius": 1.5 * mm});
            skCircle(sketch, "E48", {"center": v(-15.46, -21.67) * mm, "radius": 1.5 * mm});
            skSolve(sketch);
        }
        {
            var Q0;
            Q0=makeQuery(id+"F22.imprint","IMPRINT",FACE,{"disambiguationData":[TD([[makeQuery(id+"F22.imprint","IMPRINT",EDGE,{"derivedFrom":sQuery(id+"F22.wireOp",EDGE,"E45")}),1.0]])]});
            var Q1;
            Q1=makeQuery(id+"F22.imprint","IMPRINT",FACE,{"disambiguationData":[TD([[makeQuery(id+"F22.imprint","IMPRINT",EDGE,{"derivedFrom":sQuery(id+"F22.wireOp",EDGE,"E48")}),1.0]])]});
            var Q2;
            Q2=makeQuery(id+"F22.imprint","IMPRINT",FACE,{"disambiguationData":[TD([[makeQuery(id+"F22.imprint","IMPRINT",EDGE,{"derivedFrom":sQuery(id+"F22.wireOp",EDGE,"E46")}),1.0]])]});
            var Q3;
            Q3=makeQuery(id+"F22.imprint","IMPRINT",FACE,{"disambiguationData":[TD([[makeQuery(id+"F22.imprint","IMPRINT",EDGE,{"derivedFrom":sQuery(id+"F22.wireOp",EDGE,"E47")}),1.0]])]});
            extrude(context, id + "F23", {"entities" : qUnion([Q0, Q1, Q2, Q3]), "operationType" : NewBodyOperationType.REMOVE, "oppositeDirection" : true, "depth" : 25 * mm});
        }
        {
            var Q0;
            Q0=makeQuery(id+"F3.opExtrude","CAP_EDGE",EDGE,{"disambiguationData":[OSD([sQuery(id+"F2.wireOp",EDGE,"E20")])],"isStart":true});
            var Q1;
            Q1=makeQuery(id+"F3.opExtrude","TWEAK_EDGE",EDGE,{"derivedFrom":[makeQuery(id+"F1.opExtrude","SWEPT_FACE",FACE,{"disambiguationData":[OSD([sQuery(id+"F0.wireOp",EDGE,"E0.bottom")])]}),makeQuery(id+"F2.imprint","IMPRINT",EDGE,{"derivedFrom":sQuery(id+"F2.wireOp",EDGE,"E20")})]});
            var Q2;
            Q2=makeQuery(id+"F6.opShell","OFFSET_EDGE",EDGE,{"disambiguationData":[OSD([sQuery(id+"F2.wireOp",EDGE,"E20")])]});
            fillet(context, id + "F24", {"entities" : qUnion([Q0, Q1, Q2]), "radius" : 7 * mm, "tangentPropagation" : true, "allowEdgeOverflow" : false});
        }
        {
            var Q0;
            Q0=makeQuery(id+"F5.boolean.opBoolean","COPY",EDGE,{"derivedFrom":makeQuery(id+"F5.opExtrude","SWEPT_EDGE",EDGE,{"disambiguationData":[OSD([sQuery(id+"F4.wireOp",EDGE,"E21.bottom"),sQuery(id+"F4.wireOp",EDGE,"E21.left")])]})});
            var Q1;
            Q1=makeQuery(id+"F5.boolean.opBoolean","COPY",EDGE,{"derivedFrom":makeQuery(id+"F5.opExtrude","SWEPT_EDGE",EDGE,{"disambiguationData":[OSD([sQuery(id+"F4.wireOp",EDGE,"E21.top"),sQuery(id+"F4.wireOp",EDGE,"E21.left")])]})});
            var Q2;
            Q2=makeQuery(id+"F5.boolean.opBoolean","COPY",EDGE,{"derivedFrom":makeQuery(id+"F5.opExtrude","SWEPT_EDGE",EDGE,{"disambiguationData":[OSD([sQuery(id+"F4.wireOp",EDGE,"E21.top"),sQuery(id+"F4.wireOp",EDGE,"E21.right")])]})});
            var Q3;
            Q3=makeQuery(id+"F5.boolean.opBoolean","COPY",EDGE,{"derivedFrom":makeQuery(id+"F5.opExtrude","SWEPT_EDGE",EDGE,{"disambiguationData":[OSD([sQuery(id+"F4.wireOp",EDGE,"E21.bottom"),sQuery(id+"F4.wireOp",EDGE,"E21.right")])]})});
            fillet(context, id + "F25", {"entities" : qUnion([Q0, Q1, Q2, Q3]), "radius" : 10 * mm, "tangentPropagation" : true, "allowEdgeOverflow" : false});
        }
        {
            var Q0;
            Q0=makeQuery(id+"F3.opExtrude","SWEPT_FACE",FACE,{"disambiguationData":[OSD([sQuery(id+"F2.wireOp",EDGE,"E20")])]});
            var sketch = newSketch(context, id + "F26", { "sketchPlane" : qUnion([Q0])});
            skLineSegment(sketch, "E49.0", {"start": v(15.67, 61.86) * mm, "end": v(3.17, 61.86) * mm});
            skArc(sketch, "E50.0", {"start": v(15.67, 61.86) * mm, "mid": v(22.74, 58.93) * mm, "end": v(25.67, 51.86) * mm});
            skArc(sketch, "E51.0", {"start": v(-6.83, 51.86) * mm, "mid": v(-3.9, 58.93) * mm, "end": v(3.17, 61.86) * mm});
            skLineSegment(sketch, "E52.0", {"start": v(-6.83, 51.86) * mm, "end": v(-6.83, 8.28) * mm});
            skLineSegment(sketch, "E53.0", {"start": v(25.67, 51.86) * mm, "end": v(25.67, 8.28) * mm});
            skArc(sketch, "E54.0", {"start": v(25.67, 8.28) * mm, "mid": v(22.74, 1.2) * mm, "end": v(15.67, -1.72) * mm});
            skLineSegment(sketch, "E55.0", {"start": v(15.67, -1.72) * mm, "end": v(3.17, -1.72) * mm});
            skArc(sketch, "E56.0", {"start": v(3.17, -1.72) * mm, "mid": v(-3.9, 1.2) * mm, "end": v(-6.83, 8.28) * mm});
            skLineSegment(sketch, "E57.0", {"start": v(15.67, 62.36) * mm, "end": v(3.17, 62.36) * mm});
            skArc(sketch, "E57.1", {"start": v(-7.33, 51.86) * mm, "mid": v(-4.25, 59.28) * mm, "end": v(3.17, 62.36) * mm});
            skArc(sketch, "E57.2", {"start": v(15.67, 62.36) * mm, "mid": v(23.1, 59.28) * mm, "end": v(26.17, 51.86) * mm});
            skLineSegment(sketch, "E57.3", {"start": v(-7.33, 51.86) * mm, "end": v(-7.33, 8.28) * mm});
            skLineSegment(sketch, "E57.4", {"start": v(26.17, 51.86) * mm, "end": v(26.17, 8.28) * mm});
            skArc(sketch, "E57.5", {"start": v(26.17, 8.28) * mm, "mid": v(23.1, 0.86) * mm, "end": v(15.67, -2.22) * mm});
            skLineSegment(sketch, "E57.6", {"start": v(15.67, -2.22) * mm, "end": v(3.17, -2.22) * mm});
            skArc(sketch, "E57.7", {"start": v(3.17, -2.22) * mm, "mid": v(-4.25, 0.86) * mm, "end": v(-7.33, 8.28) * mm});
            skSolve(sketch);
        }
        {
            var Q0;
            Q0=makeQuery(id+"F26.imprint","IMPRINT",FACE,{"disambiguationData":[TD([[makeQuery(id+"F26.imprint","IMPRINT",EDGE,{"derivedFrom":sQuery(id+"F26.wireOp",EDGE,"E49.0")}),1.0]])]});
            extrude(context, id + "F27", {"entities" : qUnion([Q0]), "oppositeDirection" : true, "depth" : 2 * mm});
        }
        {
            var Q0;
            Q0=makeQuery(id+"F26.imprint","IMPRINT",FACE,{"disambiguationData":[TD([[makeQuery(id+"F26.imprint","IMPRINT",EDGE,{"derivedFrom":sQuery(id+"F26.wireOp",EDGE,"E49.0")}),-1.0]])]});
            var Q1;
            Q1=makeQuery(id+"F26.imprint","IMPRINT",FACE,{"disambiguationData":[TD([[makeQuery(id+"F26.imprint","IMPRINT",EDGE,{"derivedFrom":sQuery(id+"F26.wireOp",EDGE,"E49.0")}),1.0]])]});
            extrude(context, id + "F28", {"entities" : qUnion([Q0, Q1]), "operationType" : NewBodyOperationType.ADD, "depth" : 0.5 * mm});
        }
        {
            var Q0;
            Q0=makeQuery(id+"F10.boolean.opBoolean","COPY",EDGE,{"derivedFrom":makeQuery(id+"F10.opExtrude","CAP_EDGE",EDGE,{"disambiguationData":[OSD([sQuery(id+"F7.wireOp",EDGE,"E25")])],"isStart":true})});
            var Q1;
            Q1=makeQuery(id+"F10.boolean.opBoolean","INTERSECT",EDGE,{"derivedFrom":[makeQuery(id+"F3.opExtrude","SWEPT_FACE",FACE,{"disambiguationData":[OSD([sQuery(id+"F2.wireOp",EDGE,"E1")])]}),makeQuery(id+"F10.opExtrude","SWEPT_FACE",FACE,{"disambiguationData":[OSD([sQuery(id+"F7.wireOp",EDGE,"E25")])]})]});
            var Q2;
            Q2=makeQuery(id+"F11.boolean.opBoolean","INTERSECT",EDGE,{"derivedFrom":[makeQuery(id+"F3.opExtrude","SWEPT_FACE",FACE,{"disambiguationData":[OSD([sQuery(id+"F2.wireOp",EDGE,"E2")])]}),makeQuery(id+"F11.opExtrude","SWEPT_FACE",FACE,{"disambiguationData":[OSD([sQuery(id+"F8.wireOp",EDGE,"E33")])]})]});
            var Q3;
            Q3=makeQuery(id+"F11.boolean.opBoolean","COPY",EDGE,{"derivedFrom":makeQuery(id+"F11.opExtrude","CAP_EDGE",EDGE,{"disambiguationData":[OSD([sQuery(id+"F8.wireOp",EDGE,"E33")])],"isStart":true})});
            var Q4;
            Q4=makeQuery(id+"F12.boolean.opBoolean","COPY",EDGE,{"derivedFrom":makeQuery(id+"F12.opExtrude","CAP_EDGE",EDGE,{"disambiguationData":[OSD([sQuery(id+"F9.wireOp",EDGE,"E39")])],"isStart":true})});
            var Q5;
            Q5=makeQuery(id+"F12.boolean.opBoolean","INTERSECT",EDGE,{"derivedFrom":[makeQuery(id+"F3.opExtrude","SWEPT_FACE",FACE,{"disambiguationData":[OSD([sQuery(id+"F2.wireOp",EDGE,"E3")])]}),makeQuery(id+"F12.opExtrude","SWEPT_FACE",FACE,{"disambiguationData":[OSD([sQuery(id+"F9.wireOp",EDGE,"E39")])]})]});
            fillet(context, id + "F29", {"entities" : qUnion([Q0, Q1, Q2, Q3, Q4, Q5]), "radius" : 0.5 * mm, "tangentPropagation" : true, "allowEdgeOverflow" : false});
        }
        {
            var Q0;
            Q0=makeQuery(id+"F28.opExtrude","CAP_FACE",FACE,{"disambiguationData":[OSD([sQuery(id+"F26.wireOp",EDGE,"E57.0"),sQuery(id+"F26.wireOp",EDGE,"E57.1"),sQuery(id+"F26.wireOp",EDGE,"E57.2"),sQuery(id+"F26.wireOp",EDGE,"E57.3"),sQuery(id+"F26.wireOp",EDGE,"E57.4"),sQuery(id+"F26.wireOp",EDGE,"E57.5"),sQuery(id+"F26.wireOp",EDGE,"E57.6"),sQuery(id+"F26.wireOp",EDGE,"E57.7")])],"isStart":false});
            var Q1;
            Q1=makeQuery(id+"F27.opExtrude","CAP_FACE",FACE,{"disambiguationData":[OSD([sQuery(id+"F26.wireOp",EDGE,"E49.0"),sQuery(id+"F26.wireOp",EDGE,"E50.0"),sQuery(id+"F26.wireOp",EDGE,"E51.0"),sQuery(id+"F26.wireOp",EDGE,"E52.0"),sQuery(id+"F26.wireOp",EDGE,"E53.0"),sQuery(id+"F26.wireOp",EDGE,"E54.0"),sQuery(id+"F26.wireOp",EDGE,"E55.0"),sQuery(id+"F26.wireOp",EDGE,"E56.0")])],"isStart":false});
            fillet(context, id + "F30", {"entities" : qUnion([Q0, Q1]), "radius" : 0.3 * mm, "tangentPropagation" : true, "allowEdgeOverflow" : false});
        }
        {
            var Q0;
            Q0=makeQuery(id+"F1.opExtrude","SWEPT_BODY",BODY,{"disambiguationData":[OSD([sQuery(id+"F0.wireOp",EDGE,"E0.bottom"),sQuery(id+"F0.wireOp",EDGE,"E0.top"),sQuery(id+"F0.wireOp",EDGE,"E0.left"),sQuery(id+"F0.wireOp",EDGE,"E0.right")])]});
            var Q1;
            Q1=makeQuery(id+"F1.opExtrude","CAP_FACE",FACE,{"disambiguationData":[OSD([sQuery(id+"F0.wireOp",EDGE,"E0.bottom"),sQuery(id+"F0.wireOp",EDGE,"E0.top"),sQuery(id+"F0.wireOp",EDGE,"E0.left"),sQuery(id+"F0.wireOp",EDGE,"E0.right")])],"isStart":true});
            mirror(context, id + "F31", {"entities" : qUnion([Q0]), "mirrorPlane" : qUnion([Q1])});
        }
    });
